# Revit family: Furniture-Mirror_Cabinet-KOHLER-VERDERA-K-26382T_1
name_source: partatom
category: Casework
units: mm (PartAtom-declared; Revit-internal decimal feet)

## family parameters
Cut with Voids When Loaded = No
Host = Face
OmniClass Number = 23.21.23.17.11
OmniClass Title = Residential Cabinet
Room Calculation Point = No
Shared = No

## types (1)
- NA-Mild Silver
    ADA Compliant = No
    Assembly Code = E2010.30
    Construction Type = Wall Mount
    Date Modified = 07/27/2022
    Default Elevation = 60"
    Depth = 4 15/16"
    Description = 2.0 Mirror Cabinet (300MM, Silver, Side Cabinet)
    Finish = KOHLER-Metal-NA-Mild_Silver
    Hardware Included = No
    Height = 31 1/2"
    Manufacturer = Kohler Co.
    Master Format 2014 = 12 35 30.23
    Master Format 2014 Name = Bathroom Casework
    Material = Aluminium
    Model = K-26382T-NA
    Product Documentation Link = https://files.kohler.com.cn
    Product Finish = KOHLER-Metal-NA-Mild_Silver
    Product Name = Verdera
    Product Page URL = https://www.kohler.com.cn
    Type = 1
    URL = http://www.kohler.com.cn
    WaterSense Certified = No
    Width = 11 13/16"

## geometry (parser evidence)
native form markers: Sweep x6
no freeform markers — native parametric forms only
